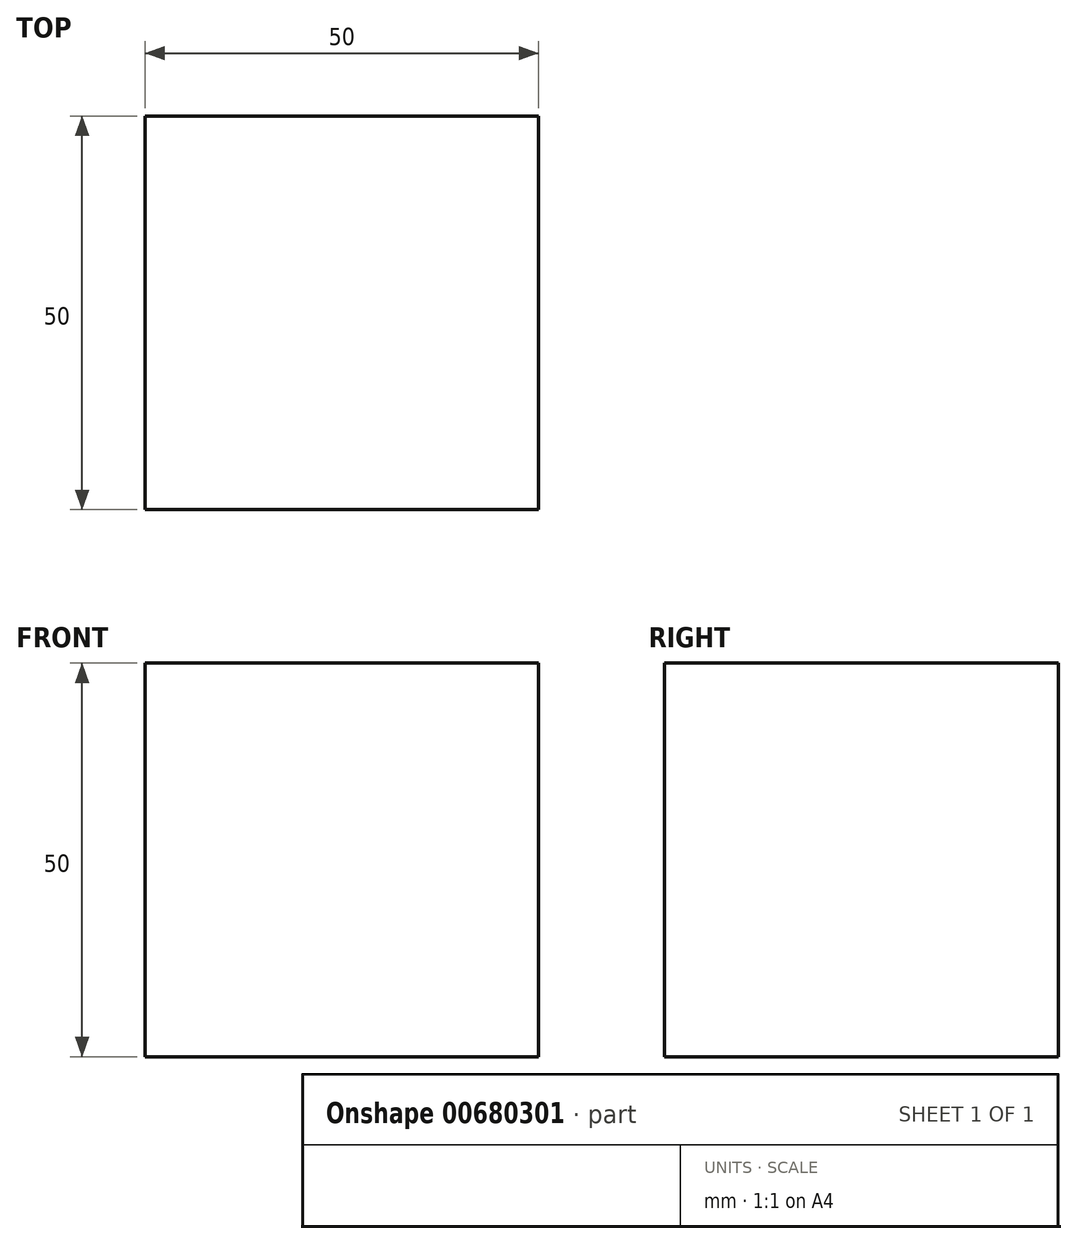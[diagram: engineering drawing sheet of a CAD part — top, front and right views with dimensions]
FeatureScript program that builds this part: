
annotation { "Feature Type Name" : "Feature", "Feature Type Description" : "" }
export const myFeature = defineFeature(function(context is Context, id is Id, definition is map)
    precondition{}
    {
        {
            var Q0;
            Q0=qCreatedBy(makeId("Top.planeOp"),FACE);
            var sketch = newSketch(context, id + "F0", { "sketchPlane" : qUnion([Q0])});
            skLineSegment(sketch, "E0.bottom", {"start": v(-1240.12, 1239.16) * mm, "end": v(29.88, 1239.16) * mm});
            skLineSegment(sketch, "E0.left", {"start": v(-1240.12, 1239.16) * mm, "end": v(-1240.12, -30.84) * mm});
            skLineSegment(sketch, "E1.bottom", {"start": v(-25, -25) * mm, "end": v(25, -25) * mm});
            skLineSegment(sketch, "E1.top", {"start": v(-25, 25) * mm, "end": v(25, 25) * mm});
            skLineSegment(sketch, "E1.left", {"start": v(-25, -25) * mm, "end": v(-25, 25) * mm});
            skLineSegment(sketch, "E1.right", {"start": v(25, -25) * mm, "end": v(25, 25) * mm});
            skPoint(sketch, "E1.middle", {"position": v(0, 0) * mm});
            skSolve(sketch);
        }
        {
            var Q0;
            Q0 = qSketchRegion(id + "F0", true);
            extrude(context, id + "F1", {"entities" : qUnion([Q0]), "depth" : 50 * mm, "offsetDistance" : 25 * mm});
        }
    });
